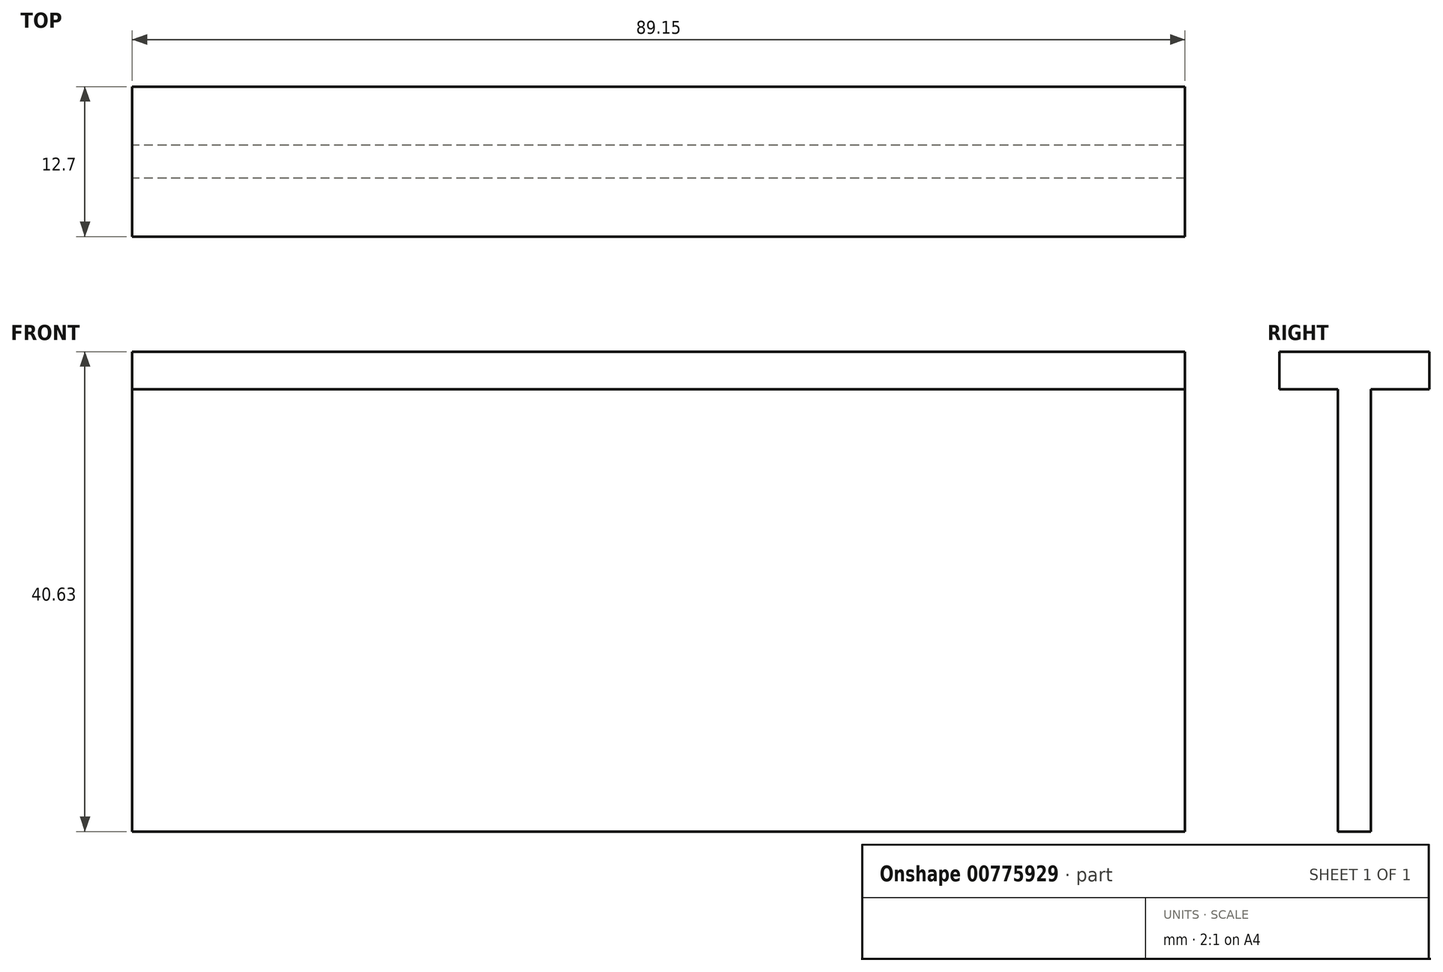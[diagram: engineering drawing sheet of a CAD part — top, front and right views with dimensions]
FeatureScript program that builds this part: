
annotation { "Feature Type Name" : "Feature", "Feature Type Description" : "" }
export const myFeature = defineFeature(function(context is Context, id is Id, definition is map)
    precondition{}
    {
        {
            var Q0;
            Q0=qCreatedBy(makeId("Right.planeOp"),FACE);
            var sketch = newSketch(context, id + "F0", { "sketchPlane" : qUnion([Q0])});
            skLineSegment(sketch, "E0", {"start": v(0, 0) * mm, "end": v(0, 3.17) * mm});
            skLineSegment(sketch, "E1", {"start": v(0, 3.17) * mm, "end": v(12.7, 3.17) * mm});
            skLineSegment(sketch, "E2", {"start": v(12.7, 3.17) * mm, "end": v(12.7, 0) * mm});
            skLineSegment(sketch, "E3", {"start": v(12.7, 0) * mm, "end": v(7.75, 0) * mm});
            skLineSegment(sketch, "E4", {"start": v(7.75, 0) * mm, "end": v(7.75, -37.47) * mm});
            skLineSegment(sketch, "E5", {"start": v(7.75, -37.47) * mm, "end": v(4.95, -37.47) * mm});
            skLineSegment(sketch, "E6", {"start": v(4.95, -37.47) * mm, "end": v(4.95, 0) * mm});
            skLineSegment(sketch, "E7", {"start": v(4.95, 0) * mm, "end": v(0, 0) * mm});
            skSolve(sketch);
        }
        {
            var Q0;
            Q0=qSketchRegion(id+"F0",true);
            extrude(context, id + "F1", {"entities" : qUnion([Q0]), "depth" : 89.15 * mm, "offsetDistance" : 25.4 * mm});
        }
    });
